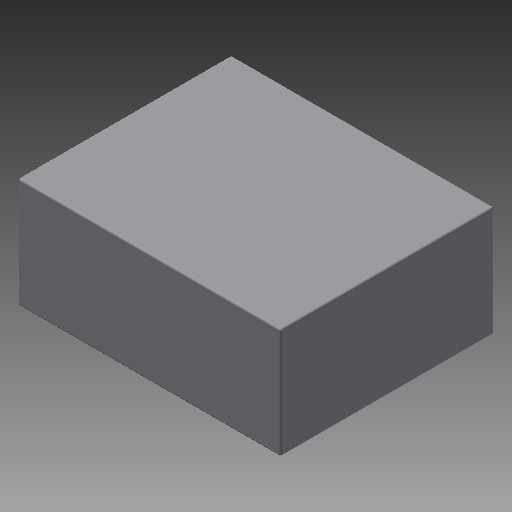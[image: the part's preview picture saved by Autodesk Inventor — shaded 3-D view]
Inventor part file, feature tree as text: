
AUTODESK INVENTOR PART (.ipt)
format: ipt  version: 2018 (Build 220112000, 112)  size: 98,304 bytes
history: native  units: in
note: dims shown in document units (in); Inventor stores cm internally (conversion verified against a paired STEP export)
features: reference x3, extrude x1, fillet x1, sketch x1
ambient origin geometry x8: Origin, YZ Plane, XZ Plane, XY Plane, X Axis, Y Axis, Z Axis, Center Point
bodies: Solid1 (feature_tree)
feature tree (6):
  extrude  "Extrusion1"  Depth=2.97in
  fillet  "Fillet1"  Radius=5.74in
  sketch  "Sketch1"  dims[d0=7.07in d1=2.97in d2=5.74in d3=0.0in d4=0.05in]
  reference  "Reference1"
  reference  "Reference2"
  reference  "Reference3"
